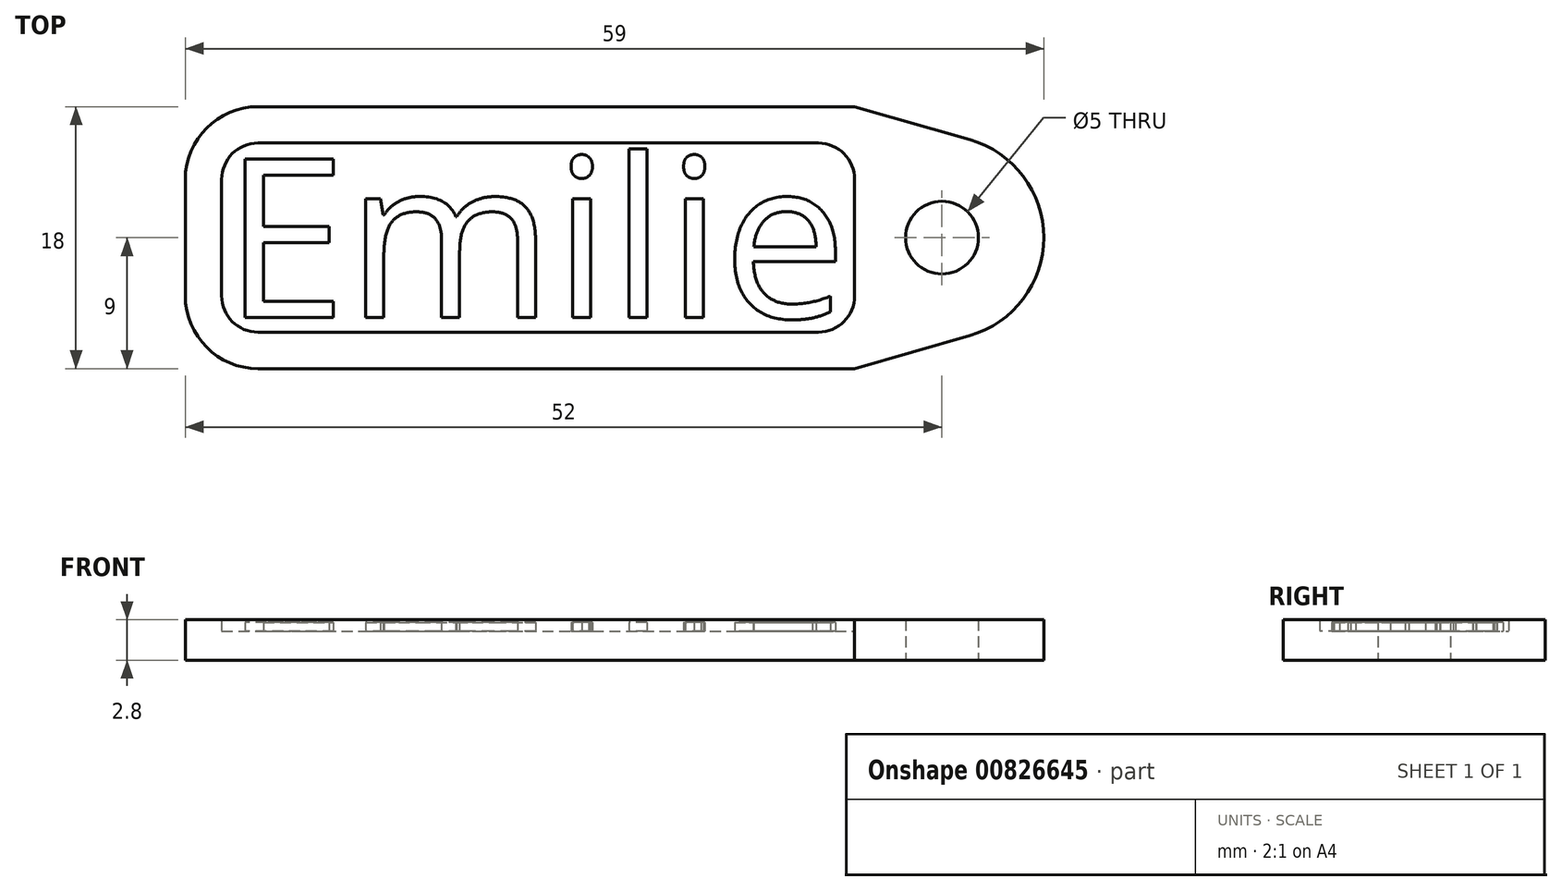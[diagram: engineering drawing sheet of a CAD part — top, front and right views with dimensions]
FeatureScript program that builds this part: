
annotation { "Feature Type Name" : "Feature", "Feature Type Description" : "" }
export const myFeature = defineFeature(function(context is Context, id is Id, definition is map)
    precondition{}
    {
        {
            var Q0;
            Q0=qCreatedBy(makeId("Top.planeOp"),FACE);
            var sketch = newSketch(context, id + "F0", { "sketchPlane" : qUnion([Q0])});
            skLineSegment(sketch, "E0", {"start": v(5, 9) * mm, "end": v(46, 9) * mm});
            skLineSegment(sketch, "E1", {"start": v(46, 9) * mm, "end": v(53.93, 6.73) * mm});
            skLineSegment(sketch, "E2", {"start": v(53.93, -6.73) * mm, "end": v(46, -9) * mm});
            skLineSegment(sketch, "E3", {"start": v(46, -9) * mm, "end": v(5, -9) * mm});
            skLineSegment(sketch, "E4", {"start": v(0, -4) * mm, "end": v(0, 4) * mm});
            skPoint(sketch, "E5.visualSharp", {"position": v(77.42, 0) * mm});
            skArc(sketch, "E5.filletArc", {"start": v(53.93, -6.73) * mm, "mid": v(59, 0) * mm, "end": v(53.93, 6.73) * mm});
            skPoint(sketch, "E6.visualSharp", {"position": v(0, 9) * mm});
            skArc(sketch, "E6.filletArc", {"start": v(5, 9) * mm, "mid": v(1.46, 7.54) * mm, "end": v(0, 4) * mm});
            skPoint(sketch, "E7.visualSharp", {"position": v(0, -9) * mm});
            skArc(sketch, "E7.filletArc", {"start": v(0, -4) * mm, "mid": v(1.46, -7.54) * mm, "end": v(5, -9) * mm});
            skSolve(sketch);
        }
        {
            var Q0;
            Q0=makeQuery(id+"F0.imprint","IMPRINT",FACE,{"disambiguationData":[TD([[makeQuery(id+"F0.imprint","IMPRINT",EDGE,{"derivedFrom":sQuery(id+"F0.wireOp",EDGE,"E0")}),-1.0]])]});
            extrude(context, id + "F1", {"entities" : qUnion([Q0]), "depth" : 2 * mm, "offsetDistance" : 25 * mm});
        }
        {
            var Q0;
            Q0=sQuery(id+"F0.wireOp",VERTEX,"E5.filletArc.center");
            var Q1;
            Q1=makeQuery(id+"F1.opExtrude","SWEPT_BODY",BODY,{"disambiguationData":[OSD([sQuery(id+"F0.wireOp",EDGE,"E0"),sQuery(id+"F0.wireOp",EDGE,"E1"),sQuery(id+"F0.wireOp",EDGE,"E2"),sQuery(id+"F0.wireOp",EDGE,"E3"),sQuery(id+"F0.wireOp",EDGE,"E4"),sQuery(id+"F0.wireOp",EDGE,"E5.filletArc"),sQuery(id+"F0.wireOp",EDGE,"E6.filletArc"),sQuery(id+"F0.wireOp",EDGE,"E7.filletArc")])]});
            hole(context, id + "F2", {"style" : HoleStyle.SIMPLE, "endStyle" : HoleEndStyle.THROUGH, "oppositeDirection" : true, "holeDiameter" : 5 * mm, "majorDiameter" : 5 * mm, "isTappedThrough" : true, "tappedDepth" : 12 * mm, "tapClearance" : 3, "locations" : qUnion([Q0]), "scope" : qUnion([Q1])});
        }
        {
            var Q0;
            Q0=makeQuery(id+"F1.opExtrude","CAP_FACE",FACE,{"disambiguationData":[OSD([sQuery(id+"F0.wireOp",EDGE,"E0"),sQuery(id+"F0.wireOp",EDGE,"E1"),sQuery(id+"F0.wireOp",EDGE,"E2"),sQuery(id+"F0.wireOp",EDGE,"E3"),sQuery(id+"F0.wireOp",EDGE,"E4"),sQuery(id+"F0.wireOp",EDGE,"E5.filletArc"),sQuery(id+"F0.wireOp",EDGE,"E6.filletArc"),sQuery(id+"F0.wireOp",EDGE,"E7.filletArc")])],"isStart":false});
            var sketch = newSketch(context, id + "F3", { "sketchPlane" : qUnion([Q0])});
            skLineSegment(sketch, "E8", {"start": v(2.5, 4) * mm, "end": v(2.5, -4) * mm});
            skLineSegment(sketch, "E9", {"start": v(5, -6.5) * mm, "end": v(43.5, -6.5) * mm});
            skLineSegment(sketch, "E10", {"start": v(46, -4) * mm, "end": v(46, 4) * mm});
            skLineSegment(sketch, "E11", {"start": v(43.5, 6.5) * mm, "end": v(5, 6.5) * mm});
            skPoint(sketch, "E12.visualSharp", {"position": v(2.5, 6.5) * mm});
            skArc(sketch, "E12.filletArc", {"start": v(5, 6.5) * mm, "mid": v(3.23, 5.77) * mm, "end": v(2.5, 4) * mm});
            skPoint(sketch, "E13.visualSharp", {"position": v(2.5, -6.5) * mm});
            skArc(sketch, "E13.filletArc", {"start": v(2.5, -4) * mm, "mid": v(3.23, -5.77) * mm, "end": v(5, -6.5) * mm});
            skPoint(sketch, "E14.visualSharp", {"position": v(46, -6.5) * mm});
            skArc(sketch, "E14.filletArc", {"start": v(43.5, -6.5) * mm, "mid": v(45.27, -5.77) * mm, "end": v(46, -4) * mm});
            skPoint(sketch, "E15.visualSharp", {"position": v(46, 6.5) * mm});
            skArc(sketch, "E15.filletArc", {"start": v(46, 4) * mm, "mid": v(45.27, 5.77) * mm, "end": v(43.5, 6.5) * mm});
            skText(sketch, "E16", { "text": "Emilie", "fontName": "OpenSans-Regular.ttf"});
            const initialGuessF3  = {"E16": [0.0026, -0.0055, 1, 0, 0.011]};
            skSetInitialGuess(sketch, initialGuessF3);
            skSolve(sketch);
        }
        {
            var Q0;
            Q0=makeQuery(id+"F3.imprint","IMPRINT",FACE,{"disambiguationData":[TD([[makeQuery(id+"F3.imprint","IMPRINT",EDGE,{"derivedFrom":sQuery(id+"F3.wireOp",EDGE,"E16.sketch_text.stroke-52")}),-1.0]])]});
            var Q1;
            Q1=makeQuery(id+"F3.imprint","IMPRINT",FACE,{"disambiguationData":[TD([[makeQuery(id+"F3.imprint","IMPRINT",EDGE,{"derivedFrom":sQuery(id+"F3.wireOp",EDGE,"E16.sketch_text.stroke-40")}),-1.0]])]});
            var Q2;
            Q2=makeQuery(id+"F3.imprint","IMPRINT",FACE,{"disambiguationData":[TD([[makeQuery(id+"F3.imprint","IMPRINT",EDGE,{"derivedFrom":sQuery(id+"F3.wireOp",EDGE,"E16.sketch_text.stroke-44")}),-1.0]])]});
            var Q3;
            Q3=makeQuery(id+"F3.imprint","IMPRINT",FACE,{"disambiguationData":[TD([[makeQuery(id+"F3.imprint","IMPRINT",EDGE,{"derivedFrom":sQuery(id+"F3.wireOp",EDGE,"E16.sketch_text.stroke-60")}),-1.0]])]});
            var Q4;
            Q4=makeQuery(id+"F3.imprint","IMPRINT",FACE,{"disambiguationData":[TD([[makeQuery(id+"F3.imprint","IMPRINT",EDGE,{"derivedFrom":sQuery(id+"F3.wireOp",EDGE,"E16.sketch_text.stroke-56")}),-1.0]])]});
            var Q5;
            Q5=makeQuery(id+"F3.imprint","IMPRINT",FACE,{"disambiguationData":[TD([[makeQuery(id+"F3.imprint","IMPRINT",EDGE,{"derivedFrom":sQuery(id+"F3.wireOp",EDGE,"E16.sketch_text.stroke-68")}),-1.0]])]});
            var Q6;
            Q6=makeQuery(id+"F3.imprint","IMPRINT",FACE,{"disambiguationData":[TD([[makeQuery(id+"F3.imprint","IMPRINT",EDGE,{"derivedFrom":sQuery(id+"F3.wireOp",EDGE,"E16.sketch_text.stroke-12")}),-1.0]])]});
            var Q7;
            Q7=makeQuery(id+"F3.imprint","IMPRINT",FACE,{"disambiguationData":[TD([[makeQuery(id+"F3.imprint","IMPRINT",EDGE,{"derivedFrom":sQuery(id+"F3.wireOp",EDGE,"E16.sketch_text.stroke-0")}),-1.0]])]});
            extrude(context, id + "F4", {"entities" : qUnion([Q0, Q1, Q2, Q3, Q4, Q5, Q6, Q7]), "operationType" : NewBodyOperationType.ADD, "depth" : .6 * mm, "offsetDistance" : 25 * mm});
        }
        {
            var Q0;
            Q0=makeQuery(id+"F3.imprint","IMPRINT",FACE,{"disambiguationData":[TD([[makeQuery(id+"F3.imprint","IMPRINT",EDGE,{"derivedFrom":sQuery(id+"F3.wireOp",EDGE,"E8")}),-1.0]])]});
            extrude(context, id + "F5", {"entities" : qUnion([Q0]), "operationType" : NewBodyOperationType.ADD, "depth" : .8 * mm, "offsetDistance" : 25 * mm});
        }
    });
